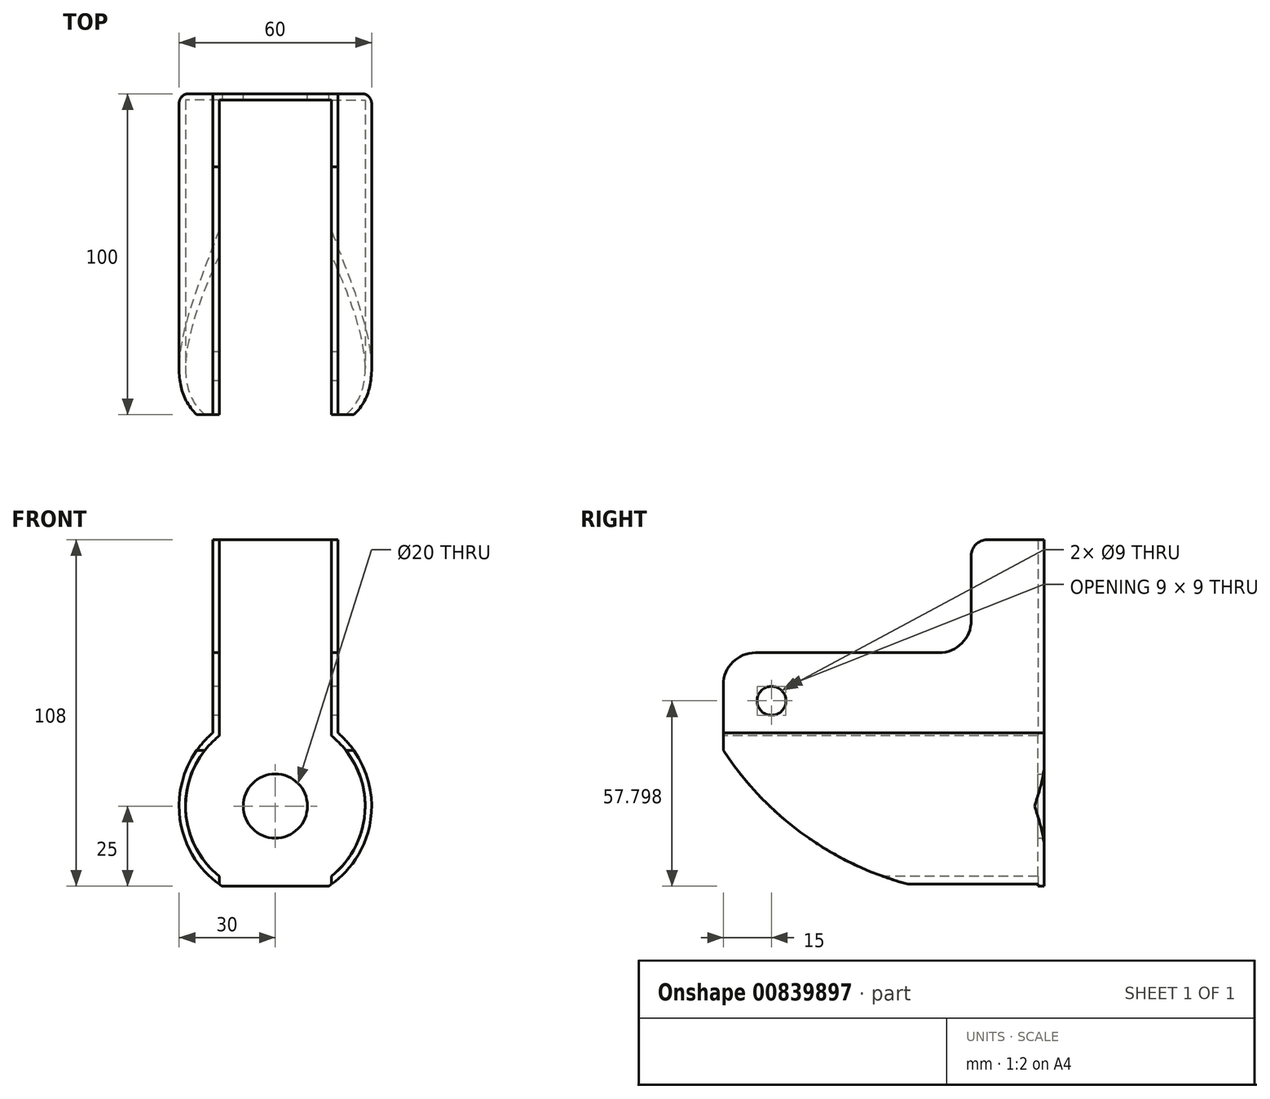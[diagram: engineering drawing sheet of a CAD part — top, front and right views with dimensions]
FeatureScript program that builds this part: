
annotation { "Feature Type Name" : "Feature", "Feature Type Description" : "" }
export const myFeature = defineFeature(function(context is Context, id is Id, definition is map)
    precondition{}
    {
        {
            var Q0;
            Q0=qCreatedBy(makeId("Top.planeOp"),FACE);
            var sketch = newSketch(context, id + "F0", { "sketchPlane" : qUnion([Q0])});
            skLineSegment(sketch, "E0.bottom", {"start": v(30, -50) * mm, "end": v(17.5, -50) * mm});
            skLineSegment(sketch, "E0.top", {"start": v(27, 50) * mm, "end": v(-27, 50) * mm});
            skLineSegment(sketch, "E0.left", {"start": v(30, -50) * mm, "end": v(30, 47) * mm});
            skLineSegment(sketch, "E0.right", {"start": v(-30, -50) * mm, "end": v(-30, 47) * mm});
            skPoint(sketch, "E0.middle", {"position": v(0, 0) * mm});
            skPoint(sketch, "E1.visualSharp", {"position": v(-30, 50) * mm});
            skArc(sketch, "E1.filletArc", {"start": v(-27, 50) * mm, "mid": v(-29.12, 49.12) * mm, "end": v(-30, 47) * mm});
            skPoint(sketch, "E2.visualSharp", {"position": v(30, 50) * mm});
            skArc(sketch, "E2.filletArc", {"start": v(30, 47) * mm, "mid": v(29.12, 49.12) * mm, "end": v(27, 50) * mm});
            skLineSegment(sketch, "E3.top", {"start": v(17.5, 48) * mm, "end": v(-17.5, 48) * mm});
            skLineSegment(sketch, "E3.left", {"start": v(17.5, -48) * mm, "end": v(17.5, 48) * mm});
            skLineSegment(sketch, "E3.right", {"start": v(-17.5, -48) * mm, "end": v(-17.5, 48) * mm});
            skLineSegment(sketch, "E4", {"start": v(17.5, -48) * mm, "end": v(17.5, -50) * mm});
            skLineSegment(sketch, "E5", {"start": v(-17.5, -48) * mm, "end": v(-17.5, -50) * mm});
            skLineSegment(sketch, "E6.trimOffspring", {"start": v(-17.5, -50) * mm, "end": v(-30, -50) * mm});
            skSolve(sketch);
        }
        {
            var Q0;
            Q0 = qSketchRegion(id + "F0", true);
            extrude(context, id + "F1", {"entities" : qUnion([Q0]), "depth" : 108 * mm, "offsetDistance" : 25 * mm});
        }
        {
            var Q0;
            Q0=makeQuery(id+"F1.opExtrude","SWEPT_FACE",FACE,{"disambiguationData":[OSD([sQuery(id+"F0.wireOp",EDGE,"E6.trimOffspring")])]});
            var sketch = newSketch(context, id + "F2", { "sketchPlane" : qUnion([Q0])});
            skLineSegment(sketch, "E7", {"start": v(-30, 25) * mm, "end": v(30, 25) * mm});
            skCircle(sketch, "E8", {"center": v(0, 25) * mm, "radius": 30 * mm});
            skLineSegment(sketch, "E9", {"start": v(30, 25) * mm, "end": v(30, 0) * mm});
            skLineSegment(sketch, "E10", {"start": v(30, 0) * mm, "end": v(16.58, 0) * mm});
            skLineSegment(sketch, "E11", {"start": v(-30, 25) * mm, "end": v(-30, 0) * mm});
            skLineSegment(sketch, "E12", {"start": v(-30, 0) * mm, "end": v(-16.58, 0) * mm});
            skSolve(sketch);
        }
        {
            var Q0;
            {var subQ0=sQuery(id+"F2.wireOp",EDGE,"E9");Q0=makeQuery(id+"F2.imprint","IMPRINT",FACE,{"disambiguationData":[TD([[makeQuery(id+"F2.imprint","IMPRINT",EDGE,{"derivedFrom":subQ0}),-1.0]])]});}
            var Q1;
            {var subQ0=sQuery(id+"F2.wireOp",EDGE,"E11");Q1=makeQuery(id+"F2.imprint","IMPRINT",FACE,{"disambiguationData":[TD([[makeQuery(id+"F2.imprint","IMPRINT",EDGE,{"derivedFrom":subQ0}),1.0]])]});}
            var Q2;
            {var subQ0=sQuery(id+"F2.wireOp",EDGE,"E12");var subQ1=sQuery(id+"F2.wireOp",EDGE,"E8");var subQ2=makeQuery(id+"F2.imprint","INTERSECT",VERTEX,{"derivedFrom":[subQ1,subQ0]});Q2=makeQuery(id+"F2.imprint","IMPRINT",FACE,{"disambiguationData":[TD([[makeQuery(id+"F2.imprint","IMPRINT",EDGE,{"disambiguationData":[TD([[subQ2,1.0]])],"derivedFrom":subQ1}),-1.0]])]});}
            extrude(context, id + "F3", {"entities" : qUnion([Q0, Q1, Q2]), "operationType" : NewBodyOperationType.REMOVE, "oppositeDirection" : true, "depth" : 150 * mm, "offsetDistance" : 25 * mm});
        }
        {
            var Q0;
            Q0=makeQuery(id+"F1.opExtrude","SWEPT_FACE",FACE,{"disambiguationData":[OSD([sQuery(id+"F0.wireOp",EDGE,"E6.trimOffspring")])]});
            var sketch = newSketch(context, id + "F4", { "sketchPlane" : qUnion([Q0])});
            skCircle(sketch, "E13", {"center": v(0, 25) * mm, "radius": 30 * mm});
            skCircle(sketch, "E14", {"center": v(0, 25) * mm, "radius": 28 * mm});
            skLineSegment(sketch, "E15", {"start": v(-19.5, 45.1) * mm, "end": v(-19.5, 108) * mm});
            skLineSegment(sketch, "E16", {"start": v(19.5, 45.1) * mm, "end": v(19.5, 108) * mm});
            skLineSegment(sketch, "E17", {"start": v(-17.5, 46.86) * mm, "end": v(-17.5, 3.14) * mm});
            skLineSegment(sketch, "E18", {"start": v(17.5, 46.86) * mm, "end": v(17.5, 3.14) * mm});
            skLineSegment(sketch, "E19", {"start": v(19.5, 108) * mm, "end": v(30, 108) * mm});
            skLineSegment(sketch, "E20", {"start": v(30, 108) * mm, "end": v(30, 25) * mm});
            skSolve(sketch);
        }
        {
            var Q0;
            {var subQ2=sQuery(id+"F4.wireOp",EDGE,"E17");Q0=makeQuery(id+"F4.imprint","IMPRINT",FACE,{"disambiguationData":[TD([[makeQuery(id+"F4.imprint","IMPRINT",EDGE,{"derivedFrom":subQ2}),-1.0]])]});}
            var Q1;
            {var subQ2=sQuery(id+"F4.wireOp",EDGE,"E18");Q1=makeQuery(id+"F4.imprint","IMPRINT",FACE,{"disambiguationData":[TD([[makeQuery(id+"F4.imprint","IMPRINT",EDGE,{"derivedFrom":subQ2}),1.0]])]});}
            extrude(context, id + "F5", {"entities" : qUnion([Q0, Q1]), "operationType" : NewBodyOperationType.REMOVE, "oppositeDirection" : true, "depth" : 98 * mm, "offsetDistance" : 25 * mm});
        }
        {
            var Q0;
            Q0=makeQuery(id+"F1.opExtrude","SWEPT_FACE",FACE,{"disambiguationData":[OSD([sQuery(id+"F0.wireOp",EDGE,"E0.left")])]});
            var sketch = newSketch(context, id + "F6", { "sketchPlane" : qUnion([Q0])});
            skLineSegment(sketch, "E21", {"start": v(-50, 0) * mm, "end": v(10, 0) * mm});
            skArc(sketch, "E22", {"start": v(-50, 42.31) * mm, "mid": v(-24.02, 15.45) * mm, "end": v(10, 0) * mm});
            skLineSegment(sketch, "E23", {"start": v(-50, 42.31) * mm, "end": v(-50, 0) * mm});
            skSolve(sketch);
        }
        {
            var Q0;
            Q0 = qSketchRegion(id + "F6", true);
            extrude(context, id + "F7", {"entities" : qUnion([Q0]), "operationType" : NewBodyOperationType.REMOVE, "oppositeDirection" : true, "depth" : 100 * mm, "offsetDistance" : 25 * mm});
        }
        {
            var Q0;
            {var subQ1=sQuery(id+"F0.wireOp",EDGE,"E6.trimOffspring");var subQ2=makeQuery(id+"F1.opExtrude","SWEPT_EDGE",EDGE,{"disambiguationData":[OSD([sQuery(id+"F0.wireOp",EDGE,"E0.right"),subQ1])]});Q0=makeQuery(id+"F4.imprint","IMPRINT",FACE,{"disambiguationData":[TD([[makeQuery(id+"F4.imprint","IMPRINT",EDGE,{"derivedFrom":subQ2}),1.0]])]});}
            var Q1;
            {var subQ4=sQuery(id+"F4.wireOp",EDGE,"E19");Q1=makeQuery(id+"F4.imprint","IMPRINT",FACE,{"disambiguationData":[TD([[makeQuery(id+"F4.imprint","IMPRINT",EDGE,{"derivedFrom":subQ4}),-1.0]])]});}
            extrude(context, id + "F8", {"entities" : qUnion([Q0, Q1]), "operationType" : NewBodyOperationType.REMOVE, "oppositeDirection" : true, "depth" : 100 * mm, "offsetDistance" : 25 * mm});
        }
        {
            var Q0;
            Q0=makeQuery(id+"F8.boolean.opBoolean","COPY",FACE,{"derivedFrom":makeQuery(id+"F8.opExtrude","SWEPT_FACE",FACE,{"disambiguationData":[OSD([sQuery(id+"F4.wireOp",EDGE,"E16")])]})});
            var sketch = newSketch(context, id + "F9", { "sketchPlane" : qUnion([Q0])});
            skLineSegment(sketch, "E24", {"start": v(-40, 72.8) * mm, "end": v(17.24, 72.8) * mm});
            skLineSegment(sketch, "E25", {"start": v(27.24, 82.8) * mm, "end": v(27.24, 103) * mm});
            skLineSegment(sketch, "E26", {"start": v(32.24, 108) * mm, "end": v(37.5, 108) * mm});
            skPoint(sketch, "E27.visualSharp", {"position": v(27.24, 72.8) * mm});
            skArc(sketch, "E27.filletArc", {"start": v(17.24, 72.8) * mm, "mid": v(24.31, 75.73) * mm, "end": v(27.24, 82.8) * mm});
            skPoint(sketch, "E28.visualSharp", {"position": v(27.24, 108) * mm});
            skArc(sketch, "E28.filletArc", {"start": v(32.24, 108) * mm, "mid": v(28.7, 106.54) * mm, "end": v(27.24, 103) * mm});
            skLineSegment(sketch, "E29", {"start": v(-50, 62.8) * mm, "end": v(-50, 47.8) * mm});
            skPoint(sketch, "E30.visualSharp", {"position": v(-50, 72.8) * mm});
            skArc(sketch, "E30.filletArc", {"start": v(-40, 72.8) * mm, "mid": v(-47.07, 69.87) * mm, "end": v(-50, 62.8) * mm});
            skSolve(sketch);
        }
        {
            var Q0;
            Q0 = qSketchRegion(id + "F9", true);
            var Q1;
            {var subQ1=sQuery(id+"F9.wireOp",EDGE,"E24");Q1=makeQuery(id+"F9.imprint","IMPRINT",FACE,{"disambiguationData":[TD([[makeQuery(id+"F9.imprint","IMPRINT",EDGE,{"derivedFrom":subQ1}),1.0]])]});}
            extrude(context, id + "F10", {"entities" : qUnion([Q0, Q1]), "operationType" : NewBodyOperationType.REMOVE, "oppositeDirection" : true, "depth" : 100 * mm, "offsetDistance" : 25 * mm});
        }
        {
            var Q0;
            Q0=makeQuery(id+"F1.opExtrude","SWEPT_FACE",FACE,{"disambiguationData":[OSD([sQuery(id+"F0.wireOp",EDGE,"E0.top")])]});
            var sketch = newSketch(context, id + "F11", { "sketchPlane" : qUnion([Q0])});
            skCircle(sketch, "E31", {"center": v(0, 25) * mm, "radius": 10 * mm});
            skSolve(sketch);
        }
        {
            var Q0;
            Q0 = qSketchRegion(id + "F11", true);
            extrude(context, id + "F12", {"entities" : qUnion([Q0]), "operationType" : NewBodyOperationType.REMOVE, "oppositeDirection" : true, "depth" : 25 * mm, "offsetDistance" : 25 * mm});
        }
        {
            var Q0;
            Q0=makeQuery(id+"F8.boolean.opBoolean","COPY",FACE,{"derivedFrom":makeQuery(id+"F8.opExtrude","SWEPT_FACE",FACE,{"disambiguationData":[OSD([sQuery(id+"F4.wireOp",EDGE,"E15")])]})});
            var sketch = newSketch(context, id + "F13", { "sketchPlane" : qUnion([Q0])});
            skCircle(sketch, "E32", {"center": v(35, 57.8) * mm, "radius": 4.5 * mm});
            skLineSegment(sketch, "E33", {"start": v(35, 57.8) * mm, "end": v(50, 57.8) * mm});
            skLineSegment(sketch, "E34", {"start": v(35, 57.8) * mm, "end": v(35, 72.8) * mm});
            skSolve(sketch);
        }
        {
            var Q0;
            Q0 = qSketchRegion(id + "F13", true);
            extrude(context, id + "F14", {"entities" : qUnion([Q0]), "operationType" : NewBodyOperationType.REMOVE, "oppositeDirection" : true, "depth" : 100 * mm, "offsetDistance" : 25 * mm});
        }
    });
